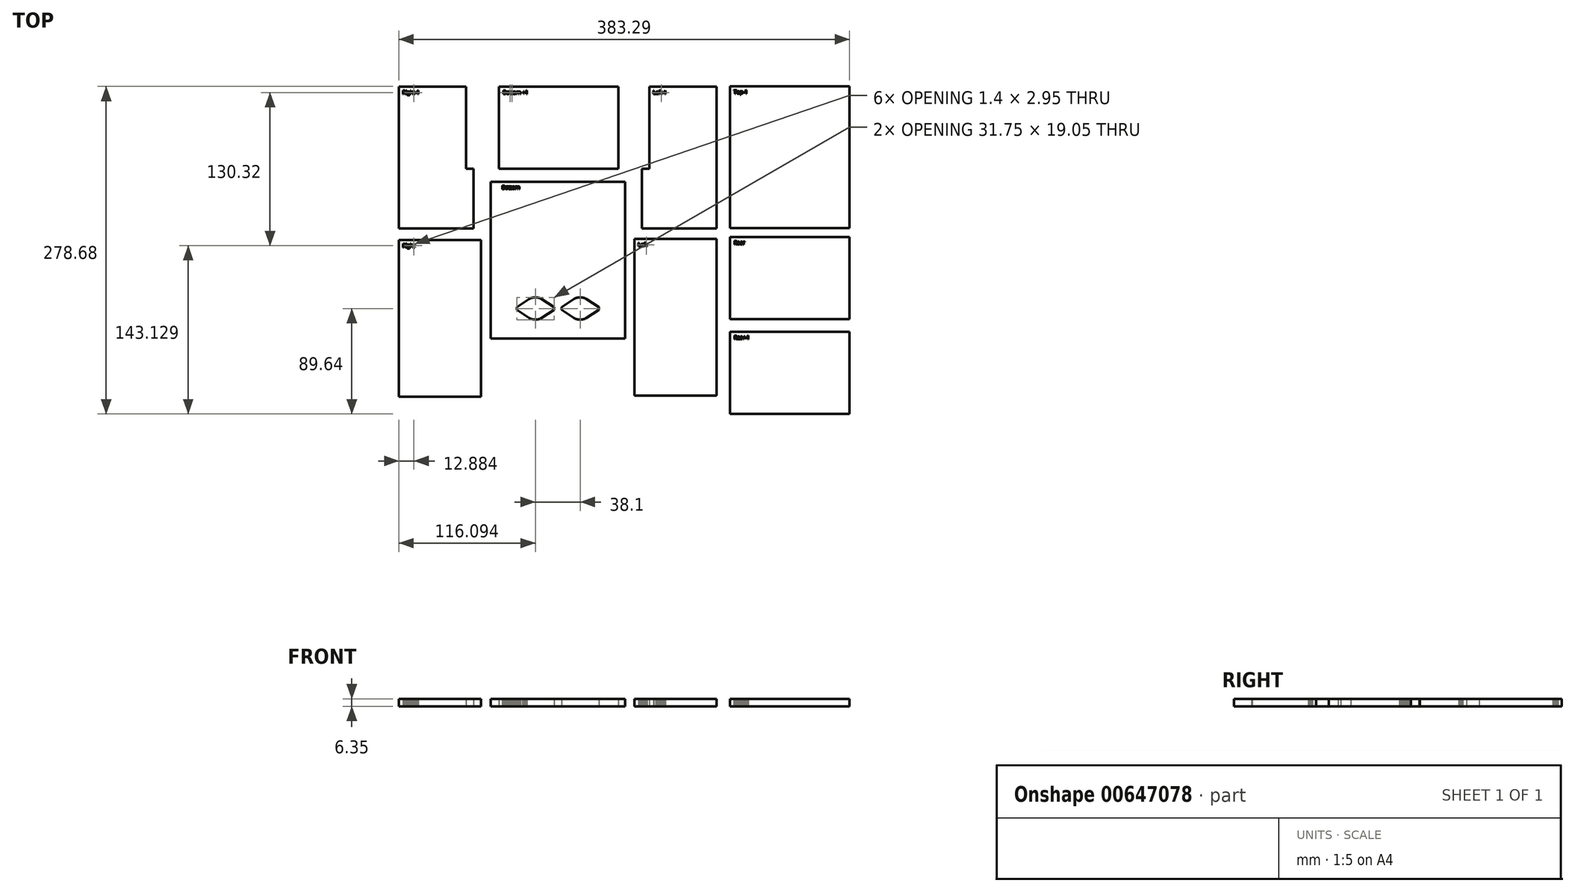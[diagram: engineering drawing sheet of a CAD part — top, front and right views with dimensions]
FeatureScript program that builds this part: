
annotation { "Feature Type Name" : "Feature", "Feature Type Description" : "" }
export const myFeature = defineFeature(function(context is Context, id is Id, definition is map)
    precondition{}
    {
        {
            var Q0;
            Q0=qCreatedBy(makeId("Top.planeOp"),FACE);
            var sketch = newSketch(context, id + "F0", { "sketchPlane" : qUnion([Q0])});
            skLineSegment(sketch, "E0.bottom", {"start": v(-51.4, -5.11) * mm, "end": v(62.9, -5.11) * mm});
            skLineSegment(sketch, "E0.top", {"start": v(-51.4, -138.46) * mm, "end": v(62.9, -138.46) * mm});
            skLineSegment(sketch, "E0.left", {"start": v(-51.4, -5.11) * mm, "end": v(-51.4, -138.46) * mm});
            skLineSegment(sketch, "E0.right", {"start": v(62.9, -5.11) * mm, "end": v(62.9, -138.46) * mm});
            skLineSegment(sketch, "E1", {"start": v(-51.4, -113.06) * mm, "end": v(-29.17, -113.06) * mm, "construction": true});
            skPoint(sketch, "E2", {"position": v(5.75, -113.06) * mm});
            skArc(sketch, "E3", {"start": v(-18.43, -121.08) * mm, "mid": v(-13.3, -122.59) * mm, "end": v(-8.16, -121.08) * mm});
            skArc(sketch, "E4", {"start": v(19.67, -121.08) * mm, "mid": v(24.8, -122.59) * mm, "end": v(29.94, -121.08) * mm});
            skPoint(sketch, "E5", {"position": v(-29.17, -113.06) * mm});
            skPoint(sketch, "E6", {"position": v(2.58, -113.06) * mm});
            skPoint(sketch, "E7", {"position": v(8.93, -113.06) * mm});
            skPoint(sketch, "E8", {"position": v(40.68, -113.06) * mm});
            skPoint(sketch, "E9", {"position": v(-22.82, -113.06) * mm});
            skPoint(sketch, "E10", {"position": v(-3.77, -113.06) * mm});
            skPoint(sketch, "E11", {"position": v(15.28, -113.06) * mm});
            skPoint(sketch, "E12", {"position": v(34.33, -113.06) * mm});
            skLineSegment(sketch, "E13", {"start": v(-29.17, -111.92) * mm, "end": v(-29.17, -114.2) * mm});
            skLineSegment(sketch, "E14", {"start": v(2.58, -111.92) * mm, "end": v(2.58, -114.2) * mm});
            skLineSegment(sketch, "E15", {"start": v(-29.17, -111.92) * mm, "end": v(-18.43, -105.04) * mm});
            skLineSegment(sketch, "E16", {"start": v(-29.17, -114.2) * mm, "end": v(-18.43, -121.08) * mm});
            skLineSegment(sketch, "E17", {"start": v(2.58, -111.92) * mm, "end": v(-8.16, -105.04) * mm});
            skLineSegment(sketch, "E18", {"start": v(2.58, -114.2) * mm, "end": v(-8.16, -121.08) * mm});
            skArc(sketch, "E19.trimOffspring", {"start": v(-8.16, -105.04) * mm, "mid": v(-13.3, -103.54) * mm, "end": v(-18.43, -105.04) * mm});
            skLineSegment(sketch, "E20", {"start": v(8.93, -111.92) * mm, "end": v(8.93, -114.2) * mm});
            skLineSegment(sketch, "E21", {"start": v(40.68, -111.92) * mm, "end": v(40.68, -114.2) * mm});
            skLineSegment(sketch, "E22", {"start": v(8.93, -111.92) * mm, "end": v(19.67, -105.04) * mm});
            skLineSegment(sketch, "E23", {"start": v(40.68, -111.92) * mm, "end": v(29.94, -105.04) * mm});
            skLineSegment(sketch, "E24", {"start": v(40.68, -114.2) * mm, "end": v(29.94, -121.08) * mm});
            skLineSegment(sketch, "E25", {"start": v(8.93, -114.2) * mm, "end": v(19.67, -121.08) * mm});
            skArc(sketch, "E26.trimOffspring", {"start": v(29.94, -105.04) * mm, "mid": v(24.8, -103.54) * mm, "end": v(19.67, -105.04) * mm});
            skLineSegment(sketch, "E27.trimOffspring", {"start": v(40.68, -113.06) * mm, "end": v(62.9, -113.06) * mm, "construction": true});
            skLineSegment(sketch, "E28.trimOffspring", {"start": v(2.58, -113.06) * mm, "end": v(8.93, -113.06) * mm, "construction": true});
            skText(sketch, "E29", { "text": "Bottom", "fontName": "OpenSans-Regular.ttf"});
            skLineSegment(sketch, "E30.bottom", {"start": v(-44.12, 75.67) * mm, "end": v(57.48, 75.67) * mm});
            skLineSegment(sketch, "E30.top", {"start": v(-44.12, 5.82) * mm, "end": v(57.48, 5.82) * mm});
            skLineSegment(sketch, "E30.left", {"start": v(-44.12, 75.67) * mm, "end": v(-44.12, 5.82) * mm});
            skLineSegment(sketch, "E30.right", {"start": v(57.48, 75.67) * mm, "end": v(57.48, 5.82) * mm});
            skText(sketch, "E31", { "text": "Bottom +1", "fontName": "OpenSans-Regular.ttf"});
            skLineSegment(sketch, "E32.bottom", {"start": v(83.56, 75.67) * mm, "end": v(140.71, 75.67) * mm});
            skLineSegment(sketch, "E32.top", {"start": v(83.56, -44.98) * mm, "end": v(140.71, -44.98) * mm});
            skLineSegment(sketch, "E32.left", {"start": v(83.56, 75.67) * mm, "end": v(83.56, 5.82) * mm});
            skLineSegment(sketch, "E32.right", {"start": v(140.71, 75.67) * mm, "end": v(140.71, -44.98) * mm});
            skLineSegment(sketch, "E33.bottom", {"start": v(70.86, -53.9) * mm, "end": v(140.71, -53.9) * mm});
            skLineSegment(sketch, "E33.top", {"start": v(70.86, -187.26) * mm, "end": v(140.71, -187.26) * mm});
            skLineSegment(sketch, "E33.left", {"start": v(70.86, -53.9) * mm, "end": v(70.86, -187.26) * mm});
            skLineSegment(sketch, "E33.right", {"start": v(140.71, -53.9) * mm, "end": v(140.71, -187.26) * mm});
            skLineSegment(sketch, "E34.bottom", {"start": v(-129.4, 75.67) * mm, "end": v(-72.24, 75.67) * mm});
            skLineSegment(sketch, "E34.top", {"start": v(-129.4, -44.98) * mm, "end": v(-72.24, -44.98) * mm});
            skLineSegment(sketch, "E34.left", {"start": v(-129.4, 75.67) * mm, "end": v(-129.4, -44.98) * mm});
            skLineSegment(sketch, "E34.right", {"start": v(-72.24, 75.67) * mm, "end": v(-72.24, 5.82) * mm});
            skLineSegment(sketch, "E35.bottom", {"start": v(-129.4, -54.66) * mm, "end": v(-59.54, -54.66) * mm});
            skLineSegment(sketch, "E35.top", {"start": v(-129.4, -188) * mm, "end": v(-59.54, -188) * mm});
            skLineSegment(sketch, "E35.left", {"start": v(-129.4, -54.66) * mm, "end": v(-129.4, -188) * mm});
            skLineSegment(sketch, "E35.right", {"start": v(-59.54, -54.66) * mm, "end": v(-59.54, -188) * mm});
            skLineSegment(sketch, "E36.bottom", {"start": v(83.56, -44.98) * mm, "end": v(77.21, -44.98) * mm});
            skLineSegment(sketch, "E36.top", {"start": v(83.56, 5.82) * mm, "end": v(77.21, 5.82) * mm});
            skLineSegment(sketch, "E36.right", {"start": v(77.21, -44.98) * mm, "end": v(77.21, 5.82) * mm});
            skLineSegment(sketch, "E37.bottom", {"start": v(-72.24, -44.98) * mm, "end": v(-65.9, -44.98) * mm});
            skLineSegment(sketch, "E37.top", {"start": v(-72.24, 5.82) * mm, "end": v(-65.9, 5.82) * mm});
            skLineSegment(sketch, "E37.right", {"start": v(-65.9, -44.98) * mm, "end": v(-65.9, 5.82) * mm});
            skLineSegment(sketch, "E38.bottom", {"start": v(152.3, 75.98) * mm, "end": v(253.9, 75.98) * mm});
            skLineSegment(sketch, "E38.top", {"start": v(152.3, -44.67) * mm, "end": v(253.9, -44.67) * mm});
            skLineSegment(sketch, "E38.left", {"start": v(152.3, 75.98) * mm, "end": v(152.3, -44.67) * mm});
            skLineSegment(sketch, "E38.right", {"start": v(253.9, 75.98) * mm, "end": v(253.9, -44.67) * mm});
            skLineSegment(sketch, "E39.bottom", {"start": v(152.3, -52.2) * mm, "end": v(253.9, -52.2) * mm});
            skLineSegment(sketch, "E39.top", {"start": v(152.3, -122.06) * mm, "end": v(253.9, -122.06) * mm});
            skLineSegment(sketch, "E39.left", {"start": v(152.3, -52.2) * mm, "end": v(152.3, -122.06) * mm});
            skLineSegment(sketch, "E39.right", {"start": v(253.9, -52.2) * mm, "end": v(253.9, -122.06) * mm});
            skLineSegment(sketch, "E40.bottom", {"start": v(152.3, -132.85) * mm, "end": v(253.9, -132.85) * mm});
            skLineSegment(sketch, "E40.top", {"start": v(152.3, -202.7) * mm, "end": v(253.9, -202.7) * mm});
            skLineSegment(sketch, "E40.left", {"start": v(152.3, -132.85) * mm, "end": v(152.3, -202.7) * mm});
            skLineSegment(sketch, "E40.right", {"start": v(253.9, -132.85) * mm, "end": v(253.9, -202.7) * mm});
            skText(sketch, "E41", { "text": "Left-1", "fontName": "OpenSans-Regular.ttf"});
            skText(sketch, "E42", { "text": "Left", "fontName": "OpenSans-Regular.ttf"});
            skText(sketch, "E43", { "text": "Top-1", "fontName": "OpenSans-Regular.ttf"});
            skText(sketch, "E44", { "text": "Right-1\n", "fontName": "OpenSans-Regular.ttf"});
            skText(sketch, "E45", { "text": "Right", "fontName": "OpenSans-Regular.ttf"});
            skText(sketch, "E46", { "text": "Rear", "fontName": "OpenSans-Regular.ttf"});
            skText(sketch, "E47", { "text": "Rear-1", "fontName": "OpenSans-Regular.ttf"});
            const initialGuessF0  = {"E29": [-0.04187, -0.01146, 1, 0, 0.00318], "E31": [-0.04095, 0.06932, 1, 0, 0.00317], "E41": [0.08674, 0.06932, 1, 0, 0.00317], "E42": [0.07404, -0.06026, 1, 0, 0.00317], "E43": [0.15548, 0.06963, 1, 0, 0.00317], "E44": [-0.12622, 0.06932, 1, 0, 0.00317], "E45": [-0.12622, -0.061, 1, 0, 0.00317], "E46": [0.15548, -0.05856, 1, 0, 0.00317], "E47": [0.15548, -0.1392, 1, 0, 0.00318]};
            skSetInitialGuess(sketch, initialGuessF0);
            skSolve(sketch);
        }
        {
            var Q0;
            Q0 = qSketchRegion(id + "F0", true);
            extrude(context, id + "F1", {"entities" : qUnion([Q0]), "depth" : 6.35 * mm, "offsetDistance" : 25 * mm});
        }
    });
